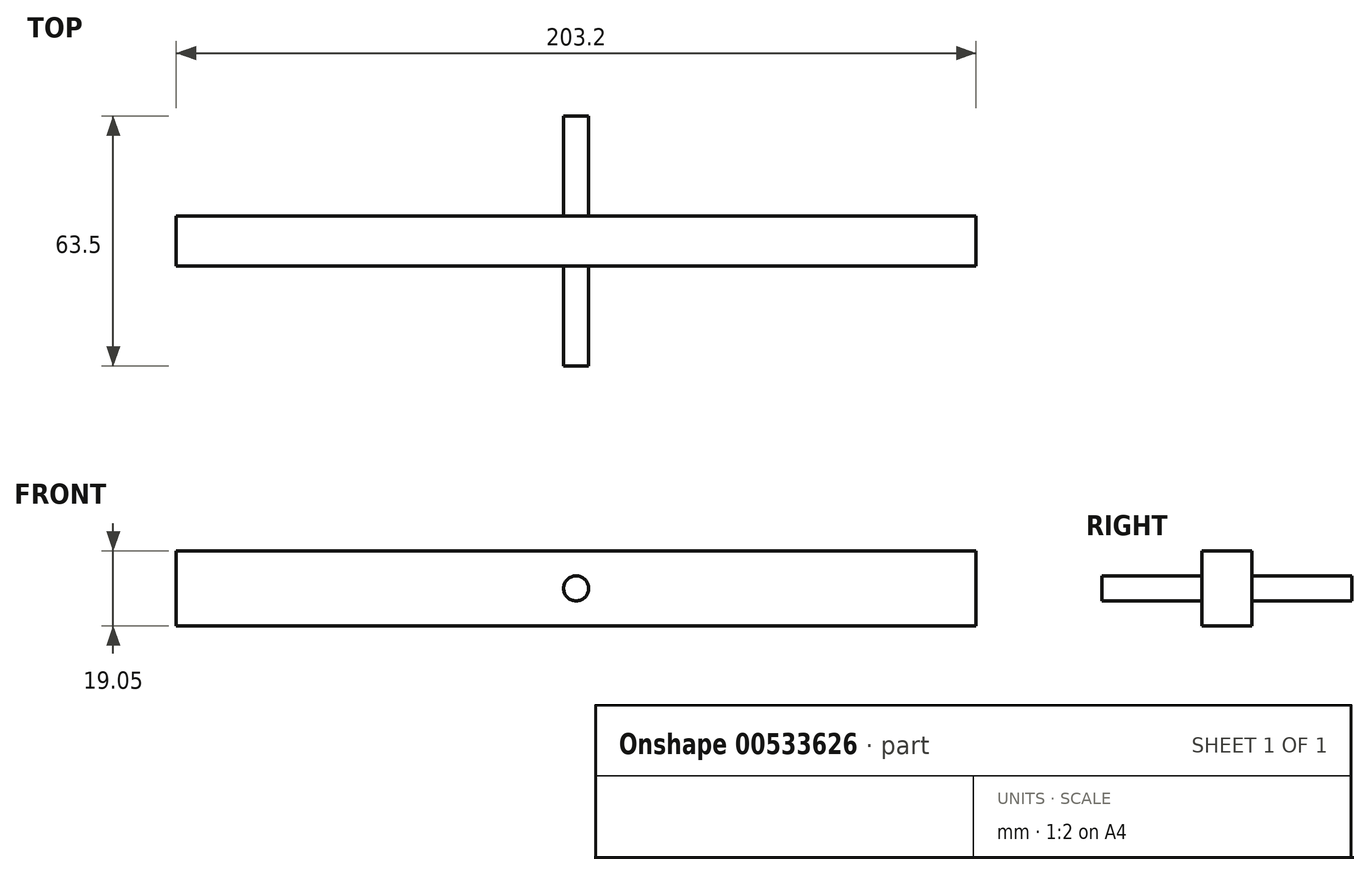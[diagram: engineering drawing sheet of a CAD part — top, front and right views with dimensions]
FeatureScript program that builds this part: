
annotation { "Feature Type Name" : "Feature", "Feature Type Description" : "" }
export const myFeature = defineFeature(function(context is Context, id is Id, definition is map)
    precondition{}
    {
        {
            var Q0;
            Q0=qCreatedBy(makeId("Top.planeOp"),FACE);
            var sketch = newSketch(context, id + "F0", { "sketchPlane" : qUnion([Q0])});
            skLineSegment(sketch, "E0.bottom", {"start": v(0, 12.7) * mm, "end": v(203.2, 12.7) * mm});
            skLineSegment(sketch, "E0.top", {"start": v(0, 0) * mm, "end": v(203.2, 0) * mm});
            skLineSegment(sketch, "E0.left", {"start": v(0, 12.7) * mm, "end": v(0, 0) * mm});
            skLineSegment(sketch, "E0.right", {"start": v(203.2, 12.7) * mm, "end": v(203.2, 0) * mm});
            skSolve(sketch);
        }
        {
            var Q0;
            Q0=makeQuery(id+"F0.imprint","IMPRINT",FACE,{"disambiguationData":[TD([[makeQuery(id+"F0.imprint","IMPRINT",EDGE,{"derivedFrom":sQuery(id+"F0.wireOp",EDGE,"E0.bottom")}),-1.0]])]});
            extrude(context, id + "F1", {"entities" : qUnion([Q0]), "depth" : 19.05 * mm, "offsetDistance" : 25.4 * mm});
        }
        {
            var Q0;
            Q0=makeQuery(id+"F1.opExtrude","SWEPT_FACE",FACE,{"disambiguationData":[OSD([sQuery(id+"F0.wireOp",EDGE,"E0.bottom")])]});
            var sketch = newSketch(context, id + "F2", { "sketchPlane" : qUnion([Q0])});
            skCircle(sketch, "E1", {"center": v(-101.6, 9.53) * mm, "radius": 3.18 * mm});
            skSolve(sketch);
        }
        {
            var Q0;
            Q0=makeQuery(id+"F2.imprint","IMPRINT",FACE,{"disambiguationData":[TD([[makeQuery(id+"F2.imprint","IMPRINT",EDGE,{"derivedFrom":sQuery(id+"F2.wireOp",EDGE,"E1")}),1.0]])]});
            extrude(context, id + "F3", {"entities" : qUnion([Q0]), "operationType" : NewBodyOperationType.ADD, "depth" : 25.4 * mm, "offsetDistance" : 25.4 * mm, "hasSecondDirection" : true, "secondDirectionOppositeDirection" : true, "secondDirectionDepth" : 38.1 * mm});
        }
    });
